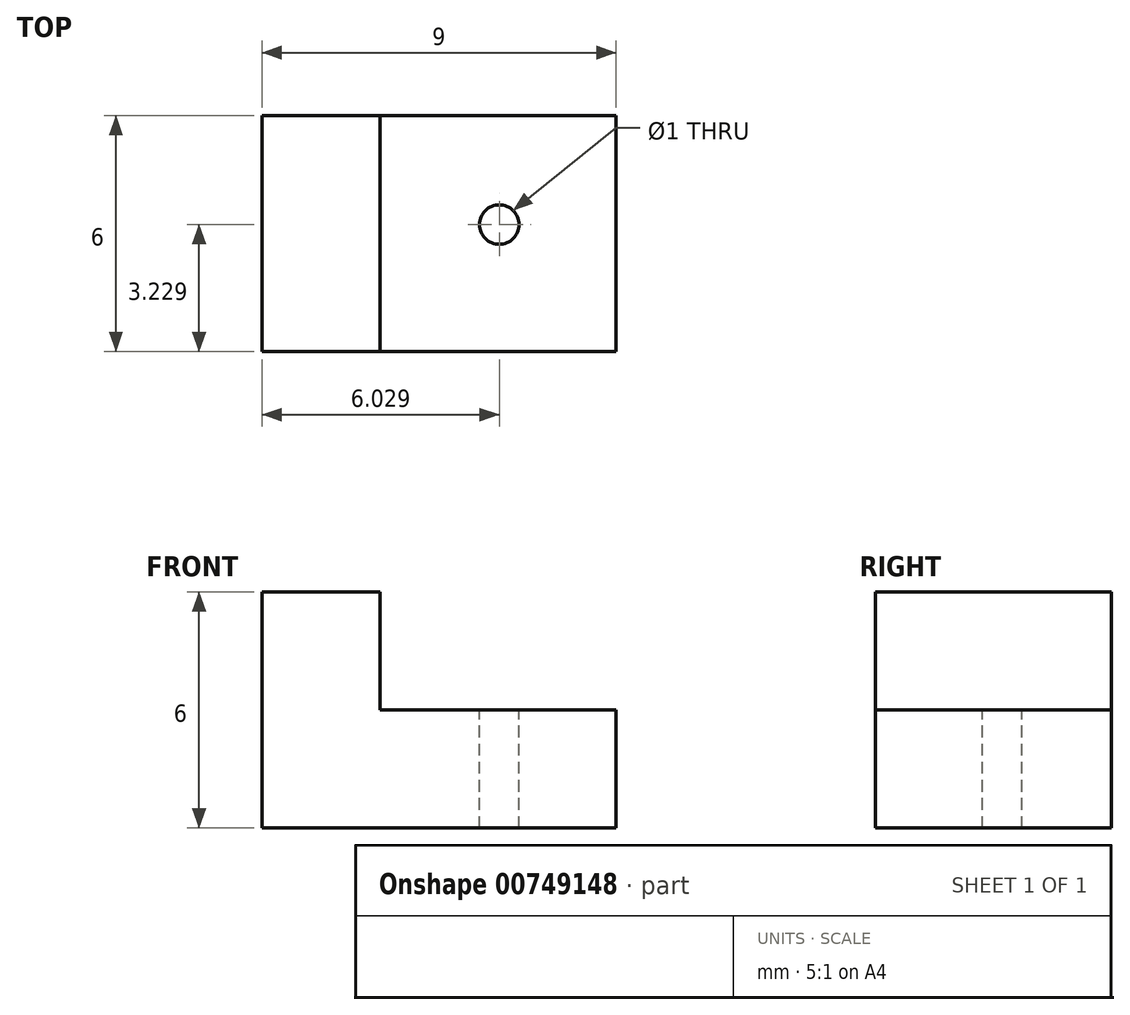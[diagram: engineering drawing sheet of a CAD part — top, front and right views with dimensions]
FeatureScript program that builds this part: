
annotation { "Feature Type Name" : "Feature", "Feature Type Description" : "" }
export const myFeature = defineFeature(function(context is Context, id is Id, definition is map)
    precondition{}
    {
        {
            var Q0;
            Q0=qCreatedBy(makeId("Front.planeOp"),FACE);
            var sketch = newSketch(context, id + "F0", { "sketchPlane" : qUnion([Q0])});
            skLineSegment(sketch, "E0.bottom", {"start": v(-4.5, -3) * mm, "end": v(4.5, -3) * mm});
            skLineSegment(sketch, "E0.top", {"start": v(-4.5, 3) * mm, "end": v(4.5, 3) * mm});
            skLineSegment(sketch, "E0.left", {"start": v(-4.5, -3) * mm, "end": v(-4.5, 3) * mm});
            skLineSegment(sketch, "E0.right", {"start": v(4.5, -3) * mm, "end": v(4.5, 3) * mm});
            skPoint(sketch, "E0.middle", {"position": v(0, 0) * mm});
            skSolve(sketch);
        }
        {
            var Q0;
            Q0=makeQuery(id+"F0.imprint","IMPRINT",FACE,{"disambiguationData":[TD([[makeQuery(id+"F0.imprint","IMPRINT",EDGE,{"derivedFrom":sQuery(id+"F0.wireOp",EDGE,"E0.bottom")}),1.0]])]});
            extrude(context, id + "F1", {"entities" : qUnion([Q0]), "depth" : 6 * mm, "offsetDistance" : 25 * mm});
        }
        {
            var Q0;
            Q0=makeQuery(id+"F1.opExtrude","CAP_FACE",FACE,{"disambiguationData":[OSD([sQuery(id+"F0.wireOp",EDGE,"E0.bottom"),sQuery(id+"F0.wireOp",EDGE,"E0.top"),sQuery(id+"F0.wireOp",EDGE,"E0.left"),sQuery(id+"F0.wireOp",EDGE,"E0.right")])],"isStart":false});
            var sketch = newSketch(context, id + "F2", { "sketchPlane" : qUnion([Q0])});
            skLineSegment(sketch, "E1.bottom", {"start": v(-1.5, 3) * mm, "end": v(4.5, 3) * mm});
            skLineSegment(sketch, "E1.top", {"start": v(-1.5, 0) * mm, "end": v(4.5, 0) * mm});
            skLineSegment(sketch, "E1.left", {"start": v(-1.5, 3) * mm, "end": v(-1.5, 0) * mm});
            skLineSegment(sketch, "E1.right", {"start": v(4.5, 3) * mm, "end": v(4.5, 0) * mm});
            skSolve(sketch);
        }
        {
            var Q0;
            Q0=makeQuery(id+"F2.imprint","IMPRINT",FACE,{"disambiguationData":[TD([[makeQuery(id+"F2.imprint","IMPRINT",EDGE,{"derivedFrom":sQuery(id+"F2.wireOp",EDGE,"E1.bottom")}),-1.0]])]});
            extrude(context, id + "F3", {"entities" : qUnion([Q0]), "operationType" : NewBodyOperationType.REMOVE, "endBound" : BoundingType.THROUGH_ALL, "oppositeDirection" : true, "depth" : 25 * mm, "offsetDistance" : 25 * mm});
        }
        {
            var Q0;
            Q0=makeQuery(id+"F3.boolean.opBoolean","COPY",FACE,{"derivedFrom":makeQuery(id+"F3.opExtrude","SWEPT_FACE",FACE,{"disambiguationData":[OSD([sQuery(id+"F2.wireOp",EDGE,"E1.top")])]})});
            var sketch = newSketch(context, id + "F4", { "sketchPlane" : qUnion([Q0])});
            skCircle(sketch, "E2", {"center": v(1.53, -2.77) * mm, "radius": 0.5 * mm});
            skSolve(sketch);
        }
        {
            var Q0;
            Q0=makeQuery(id+"F4.imprint","IMPRINT",FACE,{"disambiguationData":[TD([[makeQuery(id+"F4.imprint","IMPRINT",EDGE,{"derivedFrom":sQuery(id+"F4.wireOp",EDGE,"E2")}),1.0]])]});
            extrude(context, id + "F5", {"entities" : qUnion([Q0]), "operationType" : NewBodyOperationType.REMOVE, "endBound" : BoundingType.THROUGH_ALL, "oppositeDirection" : true, "depth" : 25 * mm, "offsetDistance" : 25 * mm});
        }
    });
